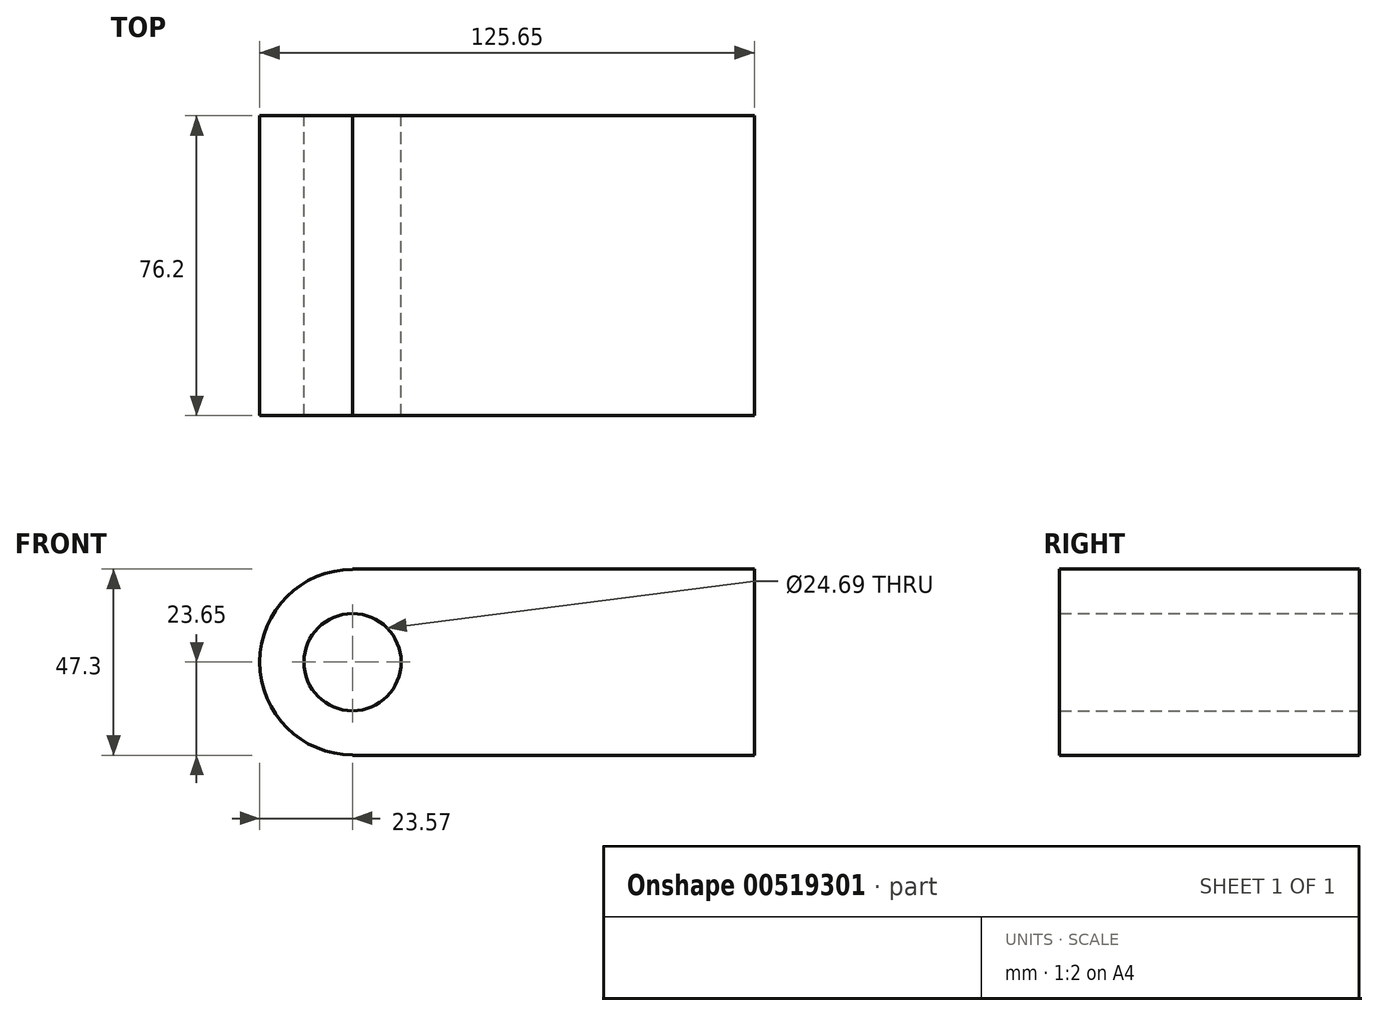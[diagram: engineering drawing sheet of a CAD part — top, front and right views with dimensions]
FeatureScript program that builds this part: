
annotation { "Feature Type Name" : "Feature", "Feature Type Description" : "" }
export const myFeature = defineFeature(function(context is Context, id is Id, definition is map)
    precondition{}
    {
        {
            var Q0;
            Q0=qCreatedBy(makeId("Front.planeOp"),FACE);
            var sketch = newSketch(context, id + "F0", { "sketchPlane" : qUnion([Q0])});
            skLineSegment(sketch, "E0.bottom", {"start": v(-51.04, -23.65) * mm, "end": v(51.04, -23.65) * mm});
            skLineSegment(sketch, "E0.top", {"start": v(-51.04, 23.65) * mm, "end": v(51.04, 23.65) * mm});
            skLineSegment(sketch, "E0.left", {"start": v(-51.04, -23.65) * mm, "end": v(-51.04, -23.57) * mm});
            skLineSegment(sketch, "E0.right", {"start": v(51.04, -23.65) * mm, "end": v(51.04, 23.65) * mm});
            skPoint(sketch, "E0.middle", {"position": v(0, 0) * mm});
            skArc(sketch, "E1", {"start": v(-51.04, 23.57) * mm, "mid": v(-74.61, 0) * mm, "end": v(-51.04, -23.57) * mm});
            skCircle(sketch, "E2", {"center": v(-51.04, 0) * mm, "radius": 12.35 * mm});
            skLineSegment(sketch, "E3.trimOffspring", {"start": v(-51.04, 23.57) * mm, "end": v(-51.04, 23.65) * mm});
            skSolve(sketch);
        }
        {
            var Q0;
            Q0=makeQuery(id+"F0.imprint","IMPRINT",FACE,{"disambiguationData":[TD([[makeQuery(id+"F0.imprint","IMPRINT",EDGE,{"derivedFrom":sQuery(id+"F0.wireOp",EDGE,"E0.bottom")}),1.0]])]});
            extrude(context, id + "F1", {"entities" : qUnion([Q0]), "depth" : 76.2 * mm, "offsetDistance" : 25.4 * mm});
        }
    });
